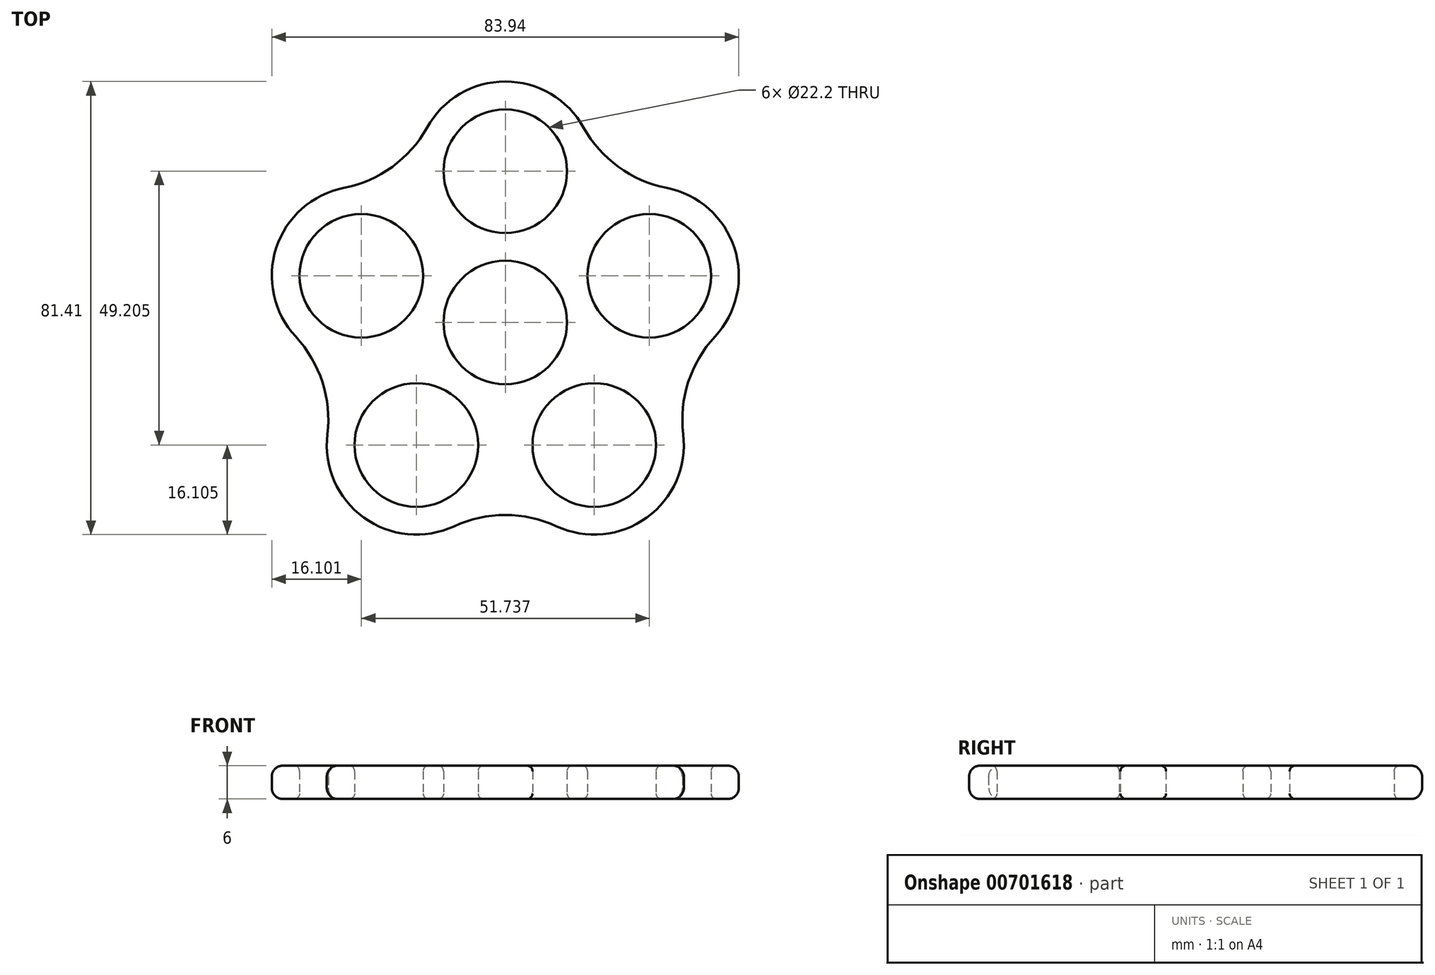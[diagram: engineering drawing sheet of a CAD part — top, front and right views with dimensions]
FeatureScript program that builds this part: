
annotation { "Feature Type Name" : "Feature", "Feature Type Description" : "" }
export const myFeature = defineFeature(function(context is Context, id is Id, definition is map)
    precondition{}
    {
        {
            var Q0;
            Q0=qCreatedBy(makeId("Top.planeOp"),FACE);
            var sketch = newSketch(context, id + "F0", { "sketchPlane" : qUnion([Q0])});
            skCircle(sketch, "E0", {"center": v(0, 0) * mm, "radius": 11.1 * mm});
            skCircle(sketch, "E1", {"center": v(0, 27.2) * mm, "radius": 11.1 * mm});
            skArc(sketch, "E2.0", {"start": v(14.07, 35.02) * mm, "mid": v(0, 43.3) * mm, "end": v(-14.07, 35.02) * mm});
            skCircle(sketch, "E3.1.0", {"center": v(-25.87, 8.4) * mm, "radius": 11.1 * mm});
            skArc(sketch, "E3.1.1", {"start": v(-28.96, 24.2) * mm, "mid": v(-41.18, 13.38) * mm, "end": v(-37.66, -2.56) * mm});
            skCircle(sketch, "E3.2.0", {"center": v(-15.99, -22) * mm, "radius": 11.1 * mm});
            skArc(sketch, "E3.2.1", {"start": v(-31.97, -20.06) * mm, "mid": v(-25.45, -35.03) * mm, "end": v(-9.2, -36.6) * mm});
            skCircle(sketch, "E3.3.0", {"center": v(15.99, -22) * mm, "radius": 11.1 * mm});
            skArc(sketch, "E3.3.1", {"start": v(9.2, -36.6) * mm, "mid": v(25.45, -35.03) * mm, "end": v(31.97, -20.06) * mm});
            skCircle(sketch, "E3.4.0", {"center": v(25.87, 8.4) * mm, "radius": 11.1 * mm});
            skArc(sketch, "E3.4.1", {"start": v(37.66, -2.56) * mm, "mid": v(41.18, 13.38) * mm, "end": v(28.96, 24.2) * mm});
            skArc(sketch, "E4", {"start": v(-28.96, 24.2) * mm, "mid": v(-20.32, 27.97) * mm, "end": v(-14.07, 35.02) * mm});
            skArc(sketch, "E5.1.0", {"start": v(-31.97, -20.06) * mm, "mid": v(-32.88, -10.68) * mm, "end": v(-37.66, -2.56) * mm});
            skArc(sketch, "E5.2.0", {"start": v(9.2, -36.6) * mm, "mid": v(0, -34.57) * mm, "end": v(-9.2, -36.6) * mm});
            skArc(sketch, "E5.3.0", {"start": v(37.66, -2.56) * mm, "mid": v(32.88, -10.68) * mm, "end": v(31.97, -20.06) * mm});
            skArc(sketch, "E5.4.0", {"start": v(14.07, 35.02) * mm, "mid": v(20.32, 27.97) * mm, "end": v(28.96, 24.2) * mm});
            skSolve(sketch);
        }
        {
            var Q0;
            Q0=makeQuery(id+"F0.imprint","IMPRINT",FACE,{"disambiguationData":[TD([[makeQuery(id+"F0.imprint","IMPRINT",EDGE,{"derivedFrom":sQuery(id+"F0.wireOp",EDGE,"E0")}),-1.0]])]});
            extrude(context, id + "F1", {"entities" : qUnion([Q0]), "depth" : 6 * mm, "offsetDistance" : 25 * mm});
        }
        {
            var Q0;
            Q0=makeQuery(id+"F1.opExtrude","CAP_EDGE",EDGE,{"disambiguationData":[OSD([sQuery(id+"F0.wireOp",EDGE,"E3.1.1")])],"isStart":false});
            var Q1;
            Q1=makeQuery(id+"F1.opExtrude","CAP_EDGE",EDGE,{"disambiguationData":[OSD([sQuery(id+"F0.wireOp",EDGE,"E5.2.0")])],"isStart":true});
            fillet(context, id + "F2", {"entities" : qUnion([Q0, Q1]), "radius" : 2 * mm, "tangentPropagation" : true, "allowEdgeOverflow" : false});
        }
        {
            var Q0;
            Q0=makeQuery(id+"F1.opExtrude","CAP_EDGE",EDGE,{"disambiguationData":[OSD([sQuery(id+"F0.wireOp",EDGE,"E3.1.0")])],"isStart":false});
            var Q1;
            Q1=makeQuery(id+"F1.opExtrude","CAP_EDGE",EDGE,{"disambiguationData":[OSD([sQuery(id+"F0.wireOp",EDGE,"E1")])],"isStart":false});
            var Q2;
            Q2=makeQuery(id+"F1.opExtrude","CAP_EDGE",EDGE,{"disambiguationData":[OSD([sQuery(id+"F0.wireOp",EDGE,"E0")])],"isStart":false});
            var Q3;
            Q3=makeQuery(id+"F1.opExtrude","CAP_EDGE",EDGE,{"disambiguationData":[OSD([sQuery(id+"F0.wireOp",EDGE,"E3.4.0")])],"isStart":false});
            var Q4;
            Q4=makeQuery(id+"F1.opExtrude","CAP_EDGE",EDGE,{"disambiguationData":[OSD([sQuery(id+"F0.wireOp",EDGE,"E3.3.0")])],"isStart":false});
            var Q5;
            Q5=makeQuery(id+"F1.opExtrude","CAP_EDGE",EDGE,{"disambiguationData":[OSD([sQuery(id+"F0.wireOp",EDGE,"E3.2.0")])],"isStart":false});
            var Q6;
            Q6=makeQuery(id+"F1.opExtrude","CAP_EDGE",EDGE,{"disambiguationData":[OSD([sQuery(id+"F0.wireOp",EDGE,"E3.3.0")])],"isStart":true});
            var Q7;
            Q7=makeQuery(id+"F1.opExtrude","CAP_EDGE",EDGE,{"disambiguationData":[OSD([sQuery(id+"F0.wireOp",EDGE,"E0")])],"isStart":true});
            var Q8;
            Q8=makeQuery(id+"F1.opExtrude","CAP_EDGE",EDGE,{"disambiguationData":[OSD([sQuery(id+"F0.wireOp",EDGE,"E3.4.0")])],"isStart":true});
            var Q9;
            Q9=makeQuery(id+"F1.opExtrude","CAP_EDGE",EDGE,{"disambiguationData":[OSD([sQuery(id+"F0.wireOp",EDGE,"E1")])],"isStart":true});
            var Q10;
            Q10=makeQuery(id+"F1.opExtrude","CAP_EDGE",EDGE,{"disambiguationData":[OSD([sQuery(id+"F0.wireOp",EDGE,"E3.1.0")])],"isStart":true});
            var Q11;
            Q11=makeQuery(id+"F1.opExtrude","CAP_EDGE",EDGE,{"disambiguationData":[OSD([sQuery(id+"F0.wireOp",EDGE,"E3.2.0")])],"isStart":true});
            fillet(context, id + "F3", {"entities" : qUnion([Q0, Q1, Q2, Q3, Q4, Q5, Q6, Q7, Q8, Q9, Q10, Q11]), "radius" : 1 * mm, "tangentPropagation" : true, "allowEdgeOverflow" : false});
        }
    });
